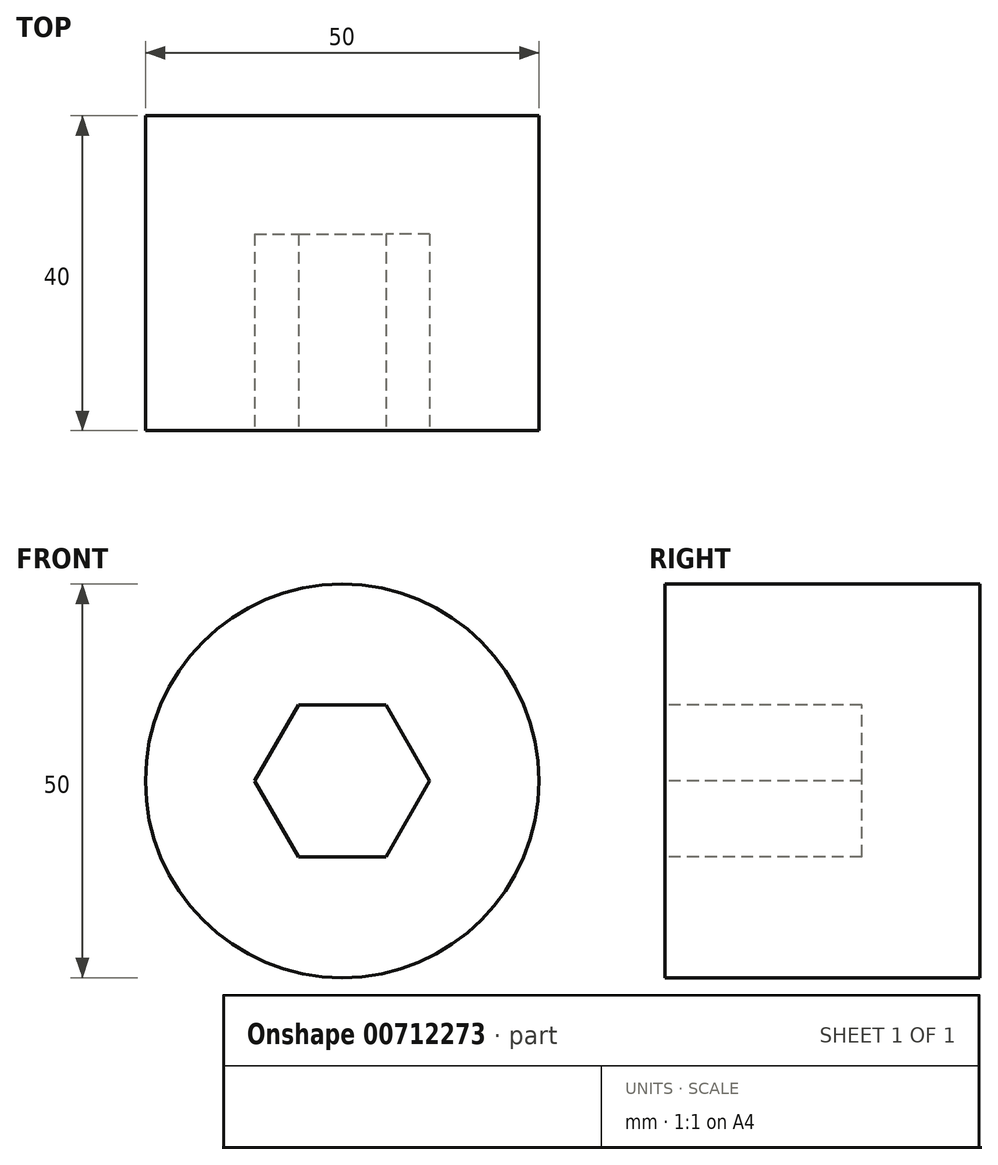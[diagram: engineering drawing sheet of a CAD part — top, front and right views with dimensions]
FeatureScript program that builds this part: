
annotation { "Feature Type Name" : "Feature", "Feature Type Description" : "" }
export const myFeature = defineFeature(function(context is Context, id is Id, definition is map)
    precondition{}
    {
        {
            var Q0;
            Q0=qCreatedBy(makeId("Front.planeOp"),FACE);
            var sketch = newSketch(context, id + "F0", { "sketchPlane" : qUnion([Q0])});
            skCircle(sketch, "E0", {"center": v(0, 0) * mm, "radius": 25 * mm});
            skSolve(sketch);
        }
        {
            var Q0;
            Q0=makeQuery(id+"F0.imprint","IMPRINT",FACE,{"disambiguationData":[TD([[makeQuery(id+"F0.imprint","IMPRINT",EDGE,{"derivedFrom":sQuery(id+"F0.wireOp",EDGE,"E0")}),1.0]])]});
            extrude(context, id + "F1", {"entities" : qUnion([Q0]), "oppositeDirection" : true, "depth" : 40 * mm, "offsetDistance" : 25 * mm});
        }
        {
            var Q0;
            Q0=qCreatedBy(makeId("Front.planeOp"),FACE);
            var sketch = newSketch(context, id + "F2", { "sketchPlane" : qUnion([Q0])});
            skCircle(sketch, "E1.cCircle", {"center": v(0, 0) * mm, "radius": 9.63 * mm, "construction": true});
            skLineSegment(sketch, "E1.0", {"start": v(-5.56, 9.63) * mm, "end": v(5.56, 9.63) * mm});
            skLineSegment(sketch, "E1.1", {"start": v(5.56, 9.63) * mm, "end": v(11.12, 0) * mm});
            skLineSegment(sketch, "E1.2", {"start": v(11.12, 0) * mm, "end": v(5.56, -9.63) * mm});
            skLineSegment(sketch, "E1.3", {"start": v(5.56, -9.63) * mm, "end": v(-5.56, -9.63) * mm});
            skLineSegment(sketch, "E1.4", {"start": v(-5.56, -9.63) * mm, "end": v(-11.12, 0) * mm});
            skLineSegment(sketch, "E1.5", {"start": v(-11.12, 0) * mm, "end": v(-5.56, 9.63) * mm});
            skPoint(sketch, "E1.0.midPoint", {"position": v(0, 9.63) * mm});
            skSolve(sketch);
        }
        {
            var Q0;
            Q0=makeQuery(id+"F2.imprint","IMPRINT",FACE,{"disambiguationData":[TD([[makeQuery(id+"F2.imprint","IMPRINT",EDGE,{"derivedFrom":sQuery(id+"F2.wireOp",EDGE,"E1.0")}),-1.0]])]});
            extrude(context, id + "F3", {"entities" : qUnion([Q0]), "operationType" : NewBodyOperationType.REMOVE, "oppositeDirection" : true, "depth" : 25 * mm, "offsetDistance" : 25 * mm});
        }
    });
